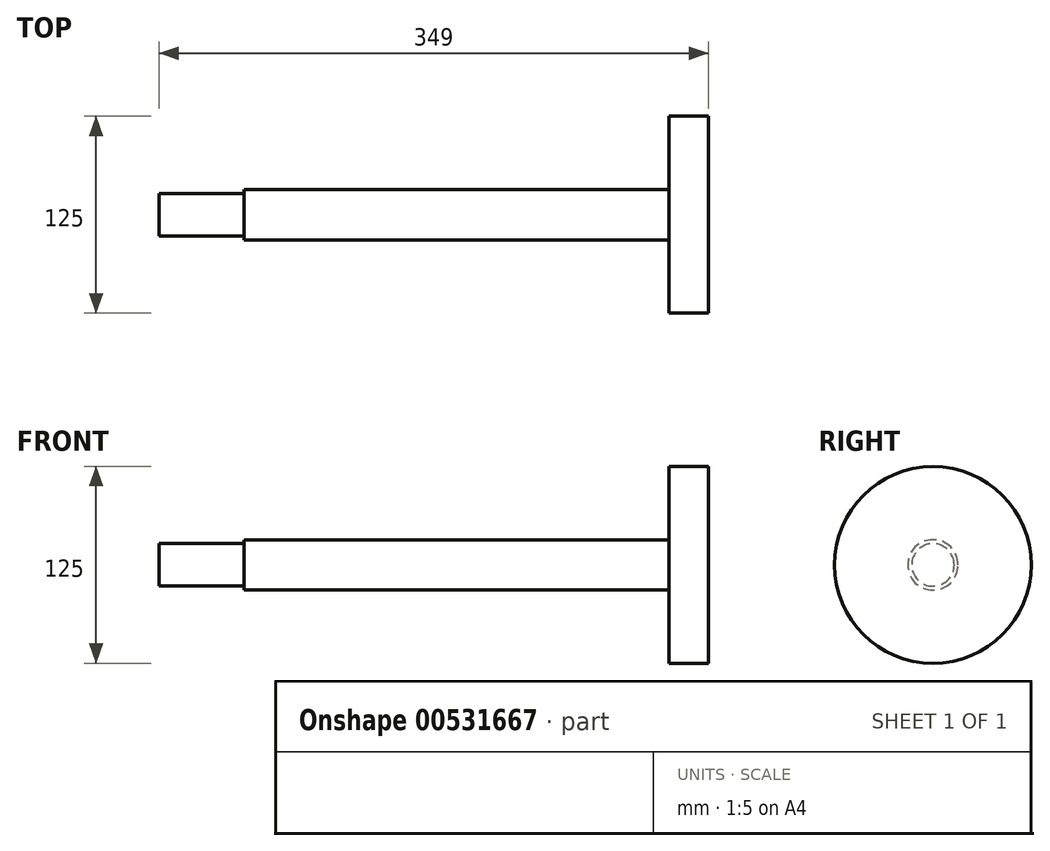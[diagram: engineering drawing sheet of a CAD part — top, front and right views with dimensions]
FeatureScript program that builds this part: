
annotation { "Feature Type Name" : "Feature", "Feature Type Description" : "" }
export const myFeature = defineFeature(function(context is Context, id is Id, definition is map)
    precondition{}
    {
        {
            var Q0;
            Q0=qCreatedBy(makeId("Front.planeOp"),FACE);
            var sketch = newSketch(context, id + "F0", { "sketchPlane" : qUnion([Q0])});
            skLineSegment(sketch, "E0", {"start": v(0, 0) * mm, "end": v(295, 0) * mm});
            skLineSegment(sketch, "E1", {"start": v(295, 0) * mm, "end": v(295, 62.5) * mm});
            skLineSegment(sketch, "E2", {"start": v(295, 62.5) * mm, "end": v(270, 62.5) * mm});
            skLineSegment(sketch, "E3", {"start": v(270, 62.5) * mm, "end": v(270, 16) * mm});
            skLineSegment(sketch, "E4", {"start": v(270, 16) * mm, "end": v(0, 16) * mm});
            skLineSegment(sketch, "E5", {"start": v(0, 0) * mm, "end": v(-54, 0) * mm});
            skLineSegment(sketch, "E6", {"start": v(-54, 0) * mm, "end": v(-54, 13.5) * mm});
            skLineSegment(sketch, "E7", {"start": v(-54, 13.5) * mm, "end": v(0, 13.5) * mm});
            skLineSegment(sketch, "E8", {"start": v(0, 13.5) * mm, "end": v(0, 16) * mm});
            skSolve(sketch);
        }
        {
            var Q0;
            Q0=makeQuery(id+"F0.imprint","IMPRINT",FACE,{"disambiguationData":[TD([[makeQuery(id+"F0.imprint","IMPRINT",EDGE,{"derivedFrom":sQuery(id+"F0.wireOp",EDGE,"E0")}),1.0]])]});
            var Q1;
            Q1=sQuery(id+"F0.wireOp",EDGE,"E0");
            revolve(context, id + "F1", {"entities" : qUnion([Q0]), "axis" : qUnion([Q1]), "revolveType" : RevolveType.FULL});
        }
    });
